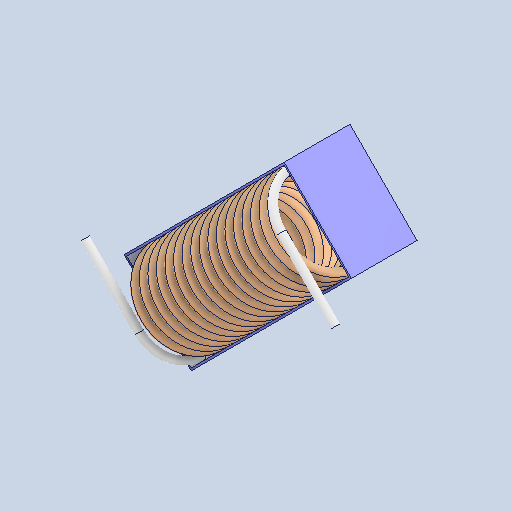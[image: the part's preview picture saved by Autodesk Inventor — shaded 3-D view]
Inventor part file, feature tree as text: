
AUTODESK INVENTOR PART (.ipt)
format: ipt  version: 2025 (Build 290162000, 162)  size: 709,632 bytes
history: native  units: mm
features: sweep x1, other x1
ambient origin geometry x8: Origin, YZ Plane, XZ Plane, XY Plane, X Axis, Y Axis, Z Axis, Center Point
bodies: Solid1 (feature_tree), Solid2 (feature_tree)
feature tree (2):
  sweep  "Sweep9"
  other  "Cut-Extrude1"
